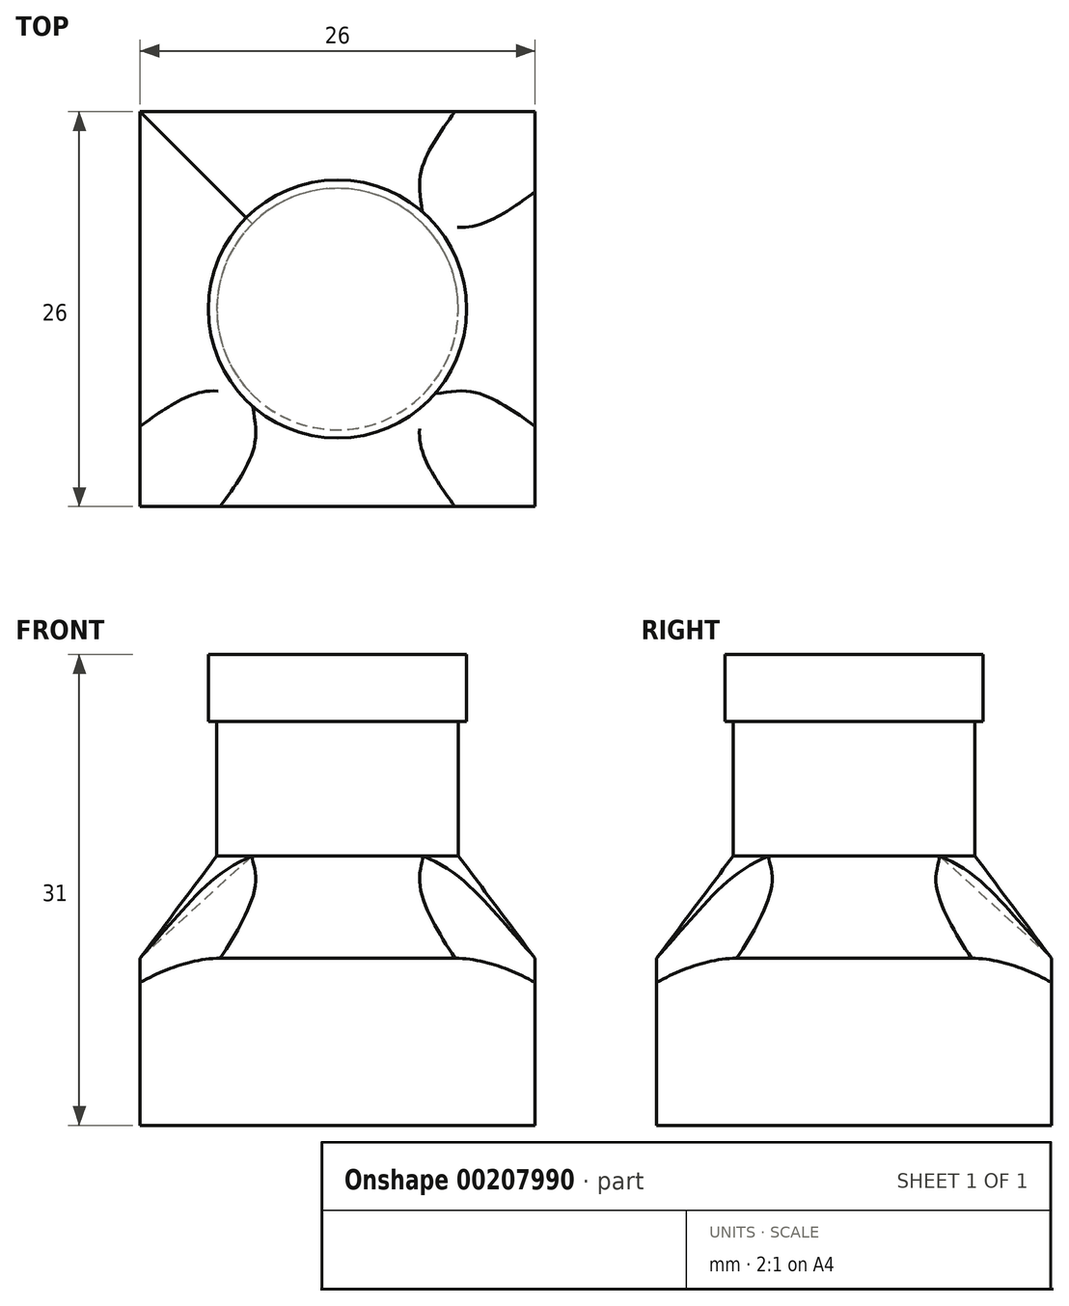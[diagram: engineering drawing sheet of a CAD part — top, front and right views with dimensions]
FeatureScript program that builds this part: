
annotation { "Feature Type Name" : "Feature", "Feature Type Description" : "" }
export const myFeature = defineFeature(function(context is Context, id is Id, definition is map)
    precondition{}
    {
        {
            var Q0;
            Q0=qCreatedBy(makeId("Top.planeOp"),FACE);
            var sketch = newSketch(context, id + "F0", { "sketchPlane" : qUnion([Q0])});
            skLineSegment(sketch, "E0.bottom", {"start": v(13, 13) * mm, "end": v(-13, 13) * mm});
            skLineSegment(sketch, "E0.top", {"start": v(13, -13) * mm, "end": v(-13, -13) * mm});
            skLineSegment(sketch, "E0.left", {"start": v(13, 13) * mm, "end": v(13, -13) * mm});
            skLineSegment(sketch, "E0.right", {"start": v(-13, 13) * mm, "end": v(-13, -13) * mm});
            skPoint(sketch, "E0.middle", {"position": v(0, 0) * mm});
            skSolve(sketch);
        }
        {
            var Q0;
            Q0 = qSketchRegion(id + "F0", true);
            extrude(context, id + "F1", {"entities" : qUnion([Q0]), "depth" : 11 * mm});
        }
        {
            var Q0;
            Q0=qCreatedBy(makeId("Top.planeOp"),FACE);
            cPlane(context, id + "F2", {"entities" : qUnion([Q0]), "cplaneType" : CPlaneType.OFFSET, "offset" : 17.75 * mm, "width" : 150 * mm, "height" : 150 * mm});
        }
        {
            var Q0;
            Q0=qCreatedBy(id+"F2.planeOp",FACE);
            var sketch = newSketch(context, id + "F3", { "sketchPlane" : qUnion([Q0])});
            skCircle(sketch, "E1", {"center": v(0, 0) * mm, "radius": 7.95 * mm});
            skSolve(sketch);
        }
        {
            var Q1;
            Q1=makeQuery(id+"F1.opExtrude","CAP_FACE",FACE,{"disambiguationData":[OSD([sQuery(id+"F0.wireOp",EDGE,"E0.bottom"),sQuery(id+"F0.wireOp",EDGE,"E0.top"),sQuery(id+"F0.wireOp",EDGE,"E0.left"),sQuery(id+"F0.wireOp",EDGE,"E0.right")])],"isStart":false});
            var Q2;
            Q2=makeQuery(id+"F3.imprint","IMPRINT",FACE,{"disambiguationData":[TD([[makeQuery(id+"F3.imprint","IMPRINT",EDGE,{"derivedFrom":sQuery(id+"F3.wireOp",EDGE,"E1")}),1.0]])]});
            loft(context, id + "F4", {"operationType" : NewBodyOperationType.ADD, "sheetProfilesArray" : [{ "sheetProfileEntities" : qUnion([Q1]) }, { "sheetProfileEntities" : qUnion([Q2]) }]});
        }
        {
            var Q0;
            Q0 = qSketchRegion(id + "F3", true);
            extrude(context, id + "F5", {"entities" : qUnion([Q0]), "operationType" : NewBodyOperationType.ADD, "depth" : 8.85 * mm});
        }
        {
            var Q0;
            Q0=qCreatedBy(makeId("Top.planeOp"),FACE);
            cPlane(context, id + "F6", {"entities" : qUnion([Q0]), "cplaneType" : CPlaneType.OFFSET, "offset" : 26.6 * mm, "width" : 150 * mm, "height" : 150 * mm});
        }
        {
            var Q0;
            Q0=qCreatedBy(id+"F6.planeOp",FACE);
            var sketch = newSketch(context, id + "F7", { "sketchPlane" : qUnion([Q0])});
            skCircle(sketch, "E2", {"center": v(0, 0) * mm, "radius": 8.5 * mm});
            skSolve(sketch);
        }
        {
            var Q0;
            Q0 = qSketchRegion(id + "F7", true);
            extrude(context, id + "F8", {"entities" : qUnion([Q0]), "operationType" : NewBodyOperationType.ADD, "depth" : 4.4 * mm});
        }
        {
            var Q0;
            Q0=makeQuery(id+"F4.opLoft","SWEPT_EDGE",EDGE,{"disambiguationData":[OSD([sQuery(id+"F0.wireOp",EDGE,"E0.bottom"),sQuery(id+"F0.wireOp",EDGE,"E0.top"),sQuery(id+"F0.wireOp",EDGE,"E0.right"),sQuery(id+"F3.wireOp",EDGE,"E1")])]});
            var Q1;
            Q1=makeQuery(id+"F4.opLoft","SWEPT_EDGE",EDGE,{"disambiguationData":[OSD([sQuery(id+"F0.wireOp",EDGE,"E0.top"),sQuery(id+"F0.wireOp",EDGE,"E0.left"),sQuery(id+"F0.wireOp",EDGE,"E0.right"),sQuery(id+"F3.wireOp",EDGE,"E1")])]});
            var Q2;
            Q2=makeQuery(id+"F4.opLoft","SWEPT_EDGE",EDGE,{"disambiguationData":[OSD([sQuery(id+"F0.wireOp",EDGE,"E0.bottom"),sQuery(id+"F0.wireOp",EDGE,"E0.left"),sQuery(id+"F0.wireOp",EDGE,"E0.right"),sQuery(id+"F3.wireOp",EDGE,"E1")])]});
            var Q3;
            Q3=makeQuery(id+"F4.opLoft","SWEPT_EDGE",EDGE,{"disambiguationData":[OSD([sQuery(id+"F0.wireOp",EDGE,"E0.bottom"),sQuery(id+"F0.wireOp",EDGE,"E0.left")])]});
            fillet(context, id + "F9", {"entities" : qUnion([Q0, Q1, Q2, Q3]), "radius" : 7 * mm, "tangentPropagation" : true, "allowEdgeOverflow" : false});
        }
    });
